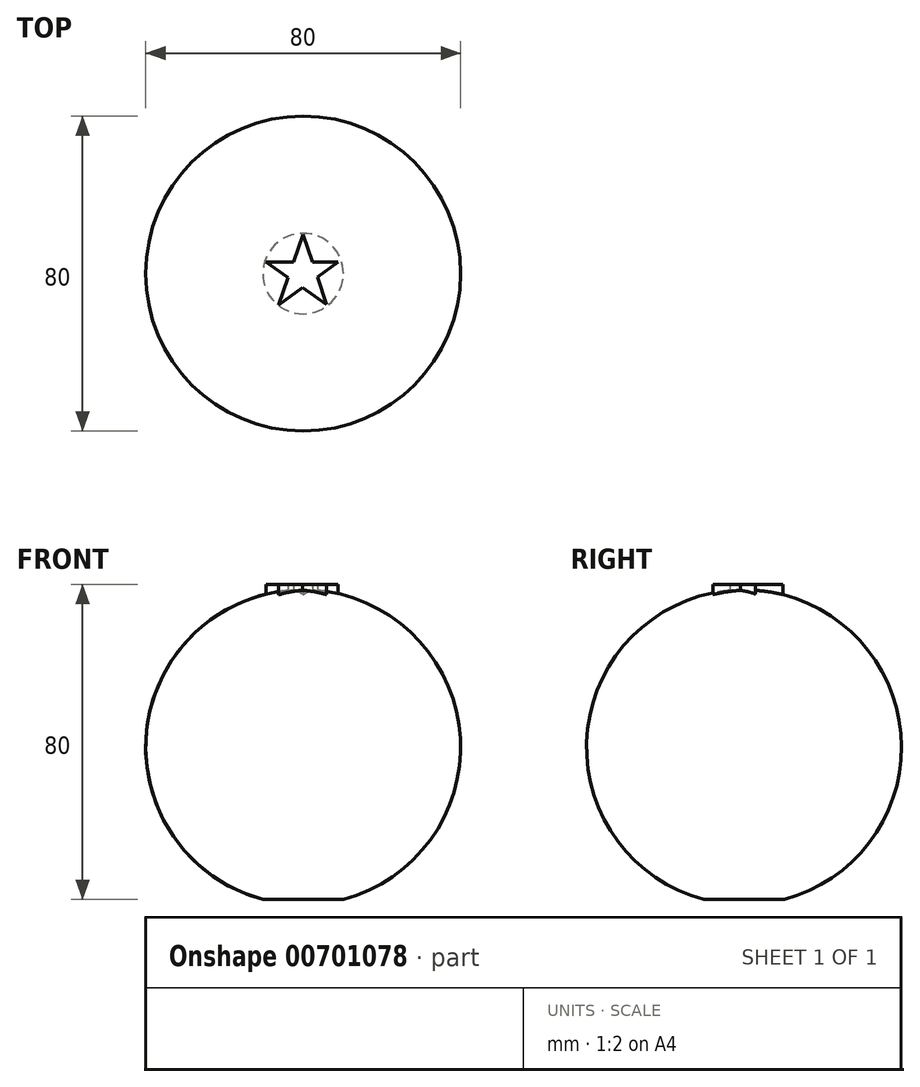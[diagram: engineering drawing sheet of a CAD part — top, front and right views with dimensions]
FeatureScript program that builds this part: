
annotation { "Feature Type Name" : "Feature", "Feature Type Description" : "" }
export const myFeature = defineFeature(function(context is Context, id is Id, definition is map)
    precondition{}
    {
        {
            var Q0;
            Q0=qCreatedBy(makeId("Front.planeOp"),FACE);
            var sketch = newSketch(context, id + "F0", { "sketchPlane" : qUnion([Q0])});
            skLineSegment(sketch, "E0", {"start": v(0, 0) * mm, "end": v(-10.22, 0) * mm});
            skArc(sketch, "E1", {"start": v(0, 78.67) * mm, "mid": v(-39.67, 43.83) * mm, "end": v(-10.22, 0) * mm});
            skLineSegment(sketch, "E2", {"start": v(-10.22, 0) * mm, "end": v(0, 0) * mm});
            skLineSegment(sketch, "E3", {"start": v(0, 0) * mm, "end": v(0, 78.67) * mm});
            skSolve(sketch);
        }
        {
            var Q0;
            Q0=makeQuery(id+"F0.imprint","IMPRINT",FACE,{"disambiguationData":[TD([[makeQuery(id+"F0.imprint","IMPRINT",EDGE,{"derivedFrom":sQuery(id+"F0.wireOp",EDGE,"E1")}),1.0]])]});
            var Q1;
            Q1=sQuery(id+"F0.wireOp",EDGE,"E3");
            revolve(context, id + "F1", {"entities" : qUnion([Q0]), "axis" : qUnion([Q1]), "revolveType" : RevolveType.FULL});
        }
        {
            var Q0;
            Q0=qCreatedBy(makeId("Top.planeOp"),FACE);
            var sketch = newSketch(context, id + "F2", { "sketchPlane" : qUnion([Q0])});
            skLineSegment(sketch, "E4", {"start": v(0, 9.9) * mm, "end": v(-2.48, 2.86) * mm});
            skLineSegment(sketch, "E5", {"start": v(0, 9.9) * mm, "end": v(2.36, 2.86) * mm});
            skLineSegment(sketch, "E6", {"start": v(5.98, -7.9) * mm, "end": v(-0.19, -3.6) * mm});
            skLineSegment(sketch, "E7", {"start": v(-9.45, 2.86) * mm, "end": v(-2.48, 2.86) * mm});
            skLineSegment(sketch, "E8", {"start": v(8.88, 2.86) * mm, "end": v(3.62, -0.88) * mm});
            skLineSegment(sketch, "E9.trimOffspring", {"start": v(-3.86, -1.04) * mm, "end": v(-6.3, -7.95) * mm});
            skLineSegment(sketch, "E10.trimOffspring", {"start": v(2.36, 2.86) * mm, "end": v(8.88, 2.86) * mm});
            skLineSegment(sketch, "E11.trimOffspring", {"start": v(3.62, -0.88) * mm, "end": v(5.98, -7.9) * mm});
            skLineSegment(sketch, "E12.trimOffspring", {"start": v(-0.19, -3.6) * mm, "end": v(-6.3, -7.95) * mm});
            skLineSegment(sketch, "E13.trimOffspring", {"start": v(-3.86, -1.04) * mm, "end": v(-9.45, 2.86) * mm});
            skSolve(sketch);
        }
        {
            var Q0;
            Q0=makeQuery(id+"F2.imprint","IMPRINT",FACE,{"disambiguationData":[TD([[makeQuery(id+"F2.imprint","IMPRINT",EDGE,{"derivedFrom":sQuery(id+"F2.wireOp",EDGE,"E4")}),1.0]])]});
            extrude(context, id + "F3", {"entities" : qUnion([Q0]), "operationType" : NewBodyOperationType.ADD, "depth" : 80 * mm, "offsetDistance" : 25 * mm});
        }
    });
